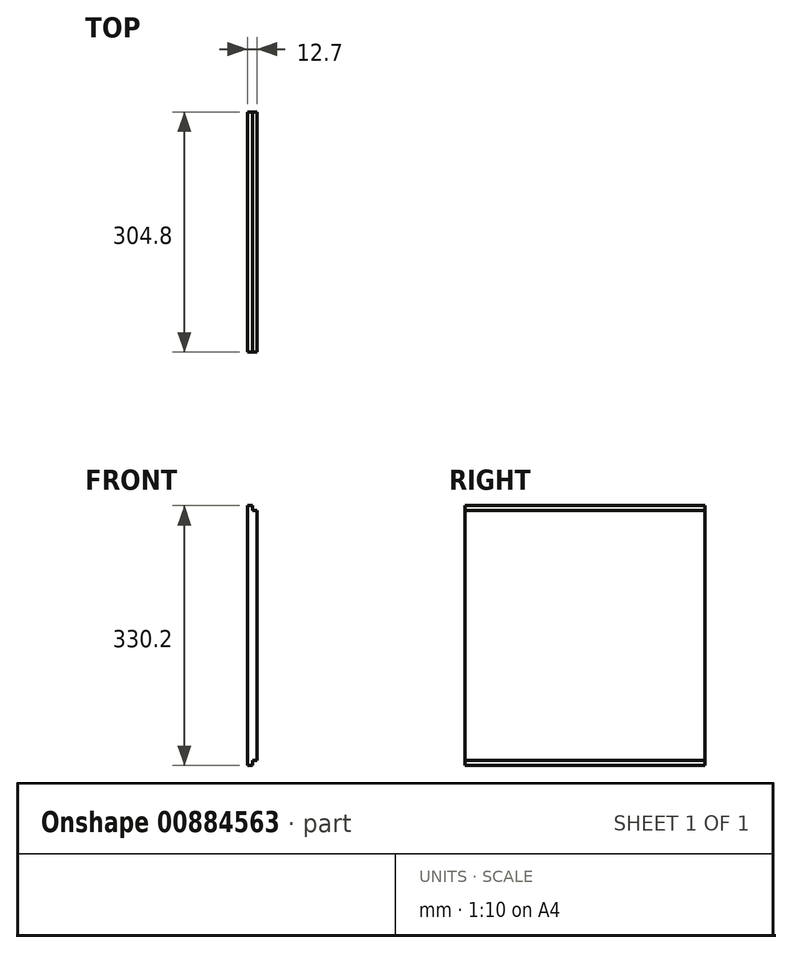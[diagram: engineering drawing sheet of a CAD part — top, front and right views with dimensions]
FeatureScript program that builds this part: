
annotation { "Feature Type Name" : "Feature", "Feature Type Description" : "" }
export const myFeature = defineFeature(function(context is Context, id is Id, definition is map)
    precondition{}
    {
        {
            var Q0;
            Q0=qCreatedBy(makeId("Right.planeOp"),FACE);
            var sketch = newSketch(context, id + "F0", { "sketchPlane" : qUnion([Q0])});
            skLineSegment(sketch, "E0.bottom", {"start": v(152.4, -165.1) * mm, "end": v(-152.4, -165.1) * mm});
            skLineSegment(sketch, "E0.top", {"start": v(152.4, 165.1) * mm, "end": v(-152.4, 165.1) * mm});
            skLineSegment(sketch, "E0.left", {"start": v(152.4, -165.1) * mm, "end": v(152.4, 165.1) * mm});
            skLineSegment(sketch, "E0.right", {"start": v(-152.4, -165.1) * mm, "end": v(-152.4, 165.1) * mm});
            skPoint(sketch, "E0.middle", {"position": v(0, 0) * mm});
            skSolve(sketch);
        }
        {
            var Q0;
            Q0 = qSketchRegion(id + "F0", true);
            extrude(context, id + "F1", {"entities" : qUnion([Q0]), "endBound" : BoundingType.SYMMETRIC, "depth" : 12.7 * mm, "offsetDistance" : 25.4 * mm});
        }
        {
            var Q0;
            Q0=qCreatedBy(makeId("Front.planeOp"),FACE);
            var sketch = newSketch(context, id + "F2", { "sketchPlane" : qUnion([Q0])});
            skLineSegment(sketch, "E1.bottom", {"start": v(0, -158.75) * mm, "end": v(6.35, -158.75) * mm});
            skLineSegment(sketch, "E1.top", {"start": v(0, -165.1) * mm, "end": v(6.35, -165.1) * mm});
            skLineSegment(sketch, "E1.left", {"start": v(0, -158.75) * mm, "end": v(0, -165.1) * mm});
            skLineSegment(sketch, "E1.right", {"start": v(6.35, -158.75) * mm, "end": v(6.35, -165.1) * mm});
            skLineSegment(sketch, "E2.MirrorCS", {"start": v(6.35, 158.75) * mm, "end": v(6.35, 165.1) * mm});
            skLineSegment(sketch, "E3.MirrorCS", {"start": v(0, 165.1) * mm, "end": v(6.35, 165.1) * mm});
            skLineSegment(sketch, "E4.MirrorCS", {"start": v(0, 158.75) * mm, "end": v(6.35, 158.75) * mm});
            skLineSegment(sketch, "E5.MirrorCS", {"start": v(0, 158.75) * mm, "end": v(0, 165.1) * mm});
            skSolve(sketch);
        }
        {
            var Q0;
            Q0 = qSketchRegion(id + "F2", true);
            extrude(context, id + "F3", {"entities" : qUnion([Q0]), "operationType" : NewBodyOperationType.REMOVE, "endBound" : BoundingType.SYMMETRIC, "depth" : 304.8 * mm, "offsetDistance" : 25.4 * mm});
        }
    });
